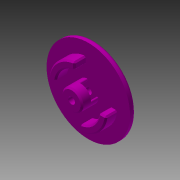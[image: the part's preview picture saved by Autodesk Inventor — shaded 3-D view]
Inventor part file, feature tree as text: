
AUTODESK INVENTOR PART (.ipt)
format: ipt  version: 2015 (Build 190159000, 159)  size: 238,080 bytes
history: native  units: in
note: dims shown in document units (in); Inventor stores cm internally (conversion verified against a paired STEP export)
features: extrude x8, sketch x8, fillet x4, pattern_circular x1, other x1, chamfer x1
ambient origin geometry x8: Origin, YZ Plane, XZ Plane, XY Plane, X Axis, Y Axis, Z Axis, Center Point
bodies: Solid1 (feature_tree)
feature tree (23):
  extrude  "Rim"  Depth=0.1in TaperAngle=0.0deg
  extrude  "nut holder"  Depth=0.3in TaperAngle=0.0deg
  extrude  "screw hole"  Depth=0.335in TaperAngle=0.0deg
  extrude  "wheel holder"  Depth=0.0478in
  pattern_circular  "wheel holder 2"  Count=2 Angle=360.0deg
  extrude  "motor holder"  Depth=0.02in
  extrude  "D-shaft mount"  Depth=0.26in TaperAngle=0.0deg
  other  "set screw work plane"
  extrude  "set screw"  Depth=0.02in
  fillet  "out side rim"  Radius=1.0in
  fillet  "screw base"  Radius=0.145in
  fillet  "screw top"  Radius=0.13in
  extrude  "nut slot"  Depth=0.02in TaperAngle=0.0deg
  chamfer  "edges removed"  Distance=0.05in
  fillet  "nut slot edges removed"  Radius=0.05in
  sketch  "Sketch1"  dims[d0=1.5in d1=0.1in d2=0.0in]
  sketch  "Sketch2"  dims[d3=0.373in d4=0.3in d5=0.0in]
  sketch  "Sketch3"  dims[d6=0.1195in d7=0.335in d8=0.0in]
  sketch  "Sketch4"  dims[d9=0.0478in d10=0.0478in]
  sketch  "Sketch5"  dims[d11=0.3925in]
  sketch  "Sketch6"  dims[d12=0.5225in]
  sketch  "Sketch7"  dims[d13=0.2in d14=0.0in d15=0.7874in d16=360.0deg]
  sketch  "Sketch8"  dims[d18=0.152in d19=0.182in d20=0.26in d21=0.0in d22=0.125in d23=1.0in d24=0.0in d25=0.145in d26=0.13in d27=0.25in d28=0.0in d29=0.05in d30=0.05in d31=0.05in d32=0.233in d33=0.138in d34=0.0in d35=0.025in d36=0.125in d37=45.0deg d43=0.02in]
